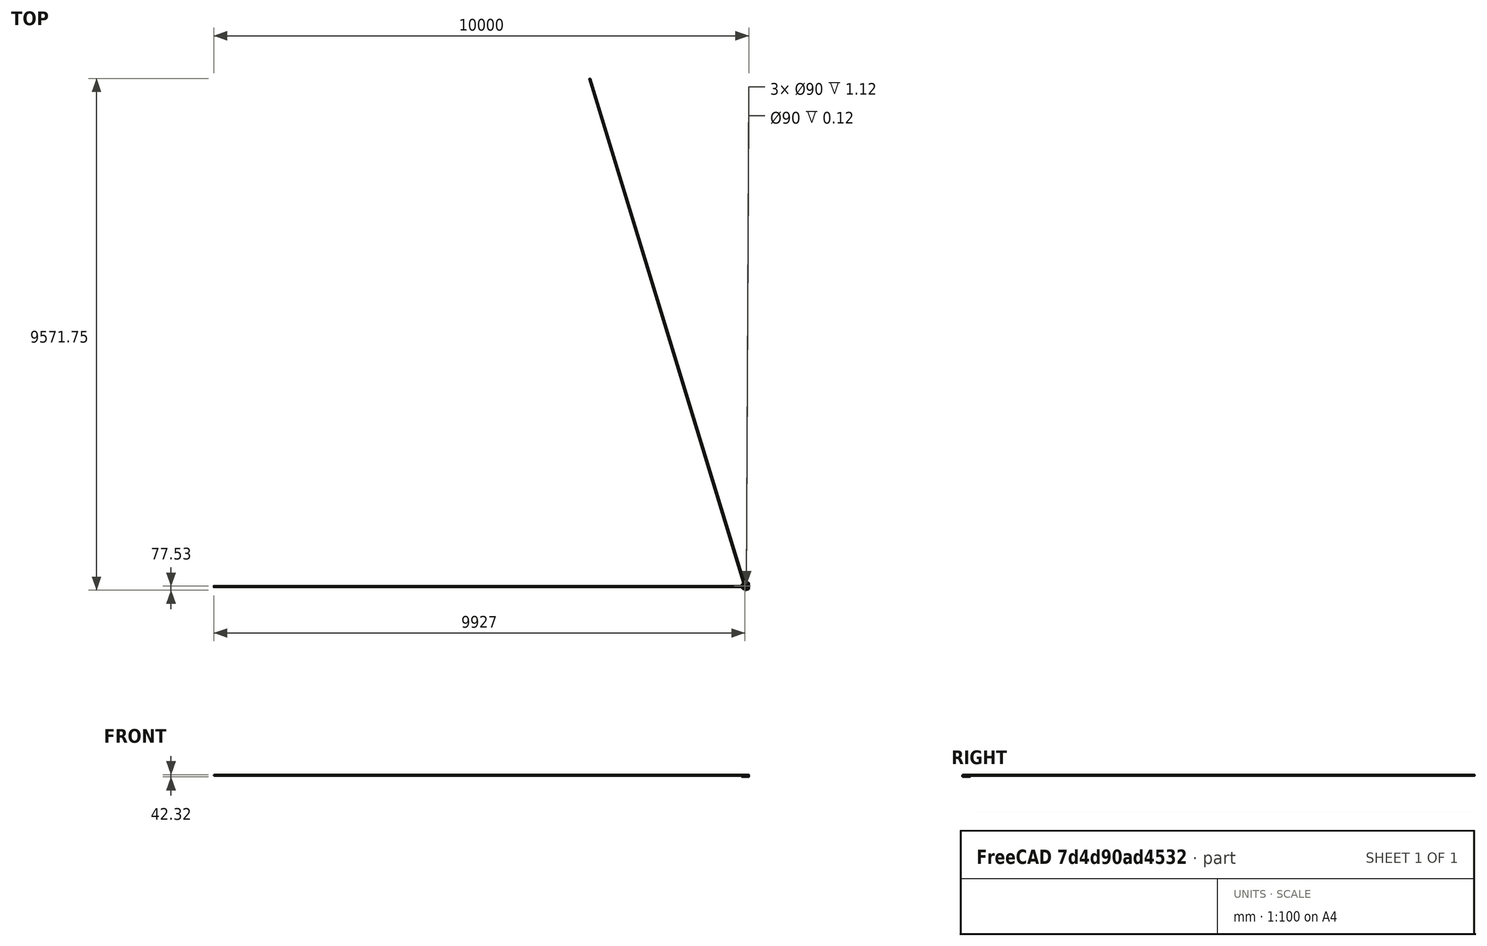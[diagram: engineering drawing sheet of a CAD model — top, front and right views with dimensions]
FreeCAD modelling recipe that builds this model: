
FCSTD DOCUMENT  (FreeCAD 0.16R)
Label: chainguard25TRev1.V4
License: All rights reserved
LicenseURL: http://en.wikipedia.org/wiki/All_rights_reserved
objects: Sketcher::SketchObject×10, PartDesign::Fillet×8, PartDesign::Pad×5, PartDesign::Pocket×5, Part::FeaturePython×3, Mesh::Feature×3
note: 41 computed .brp shape members not serialized (recipe doc carries the construction recipe); baked Part::Feature solids carry a one-line shape summary decoded from their .brp

FEATURE [Sketcher::SketchObject] Sketch001
  sketch-geometry (7):
    g0: LineSegment StartX=60 StartY=64 StartZ=0 EndX=0 EndY=64 EndZ=0
    g1: LineSegment StartX=60 StartY=-64 StartZ=0 EndX=0 EndY=-64 EndZ=0
    g2: ArcOfCircle CenterX=8.21903e-05 CenterY=0 CenterZ=0 NormalX=0 NormalY=0 NormalZ=1 Radius=64 StartAngle=1.5708 EndAngle=4.71239
    g3: Circle CenterX=0 CenterY=0 CenterZ=0 NormalX=0 NormalY=0 NormalZ=1 Radius=45
    g4: ArcOfCircle CenterX=60 CenterY=51 CenterZ=0 NormalX=0 NormalY=0 NormalZ=1 Radius=13 StartAngle=0 EndAngle=1.5708
    g5: ArcOfCircle CenterX=60 CenterY=-51 CenterZ=0 NormalX=0 NormalY=0 NormalZ=1 Radius=13 StartAngle=4.71239 EndAngle=6.28319
    g6: LineSegment StartX=73 StartY=51 StartZ=0 EndX=73 EndY=-51 EndZ=0
  constraints (23):
    c: Horizontal(g0)
    c: Horizontal(g1)
    c: Coincident(g2,g1)
    c: Coincident(g0,g2)
    c: DistanceX(g1,g0) = 0
    c: Equal(g0,g1)
    c: DistanceY(g1,g0) = 128
    c: Radius(g2) = 64
    c: Symmetric(g1,g0,g-1)
    c: Radius(g3) = 45
    c: Coincident(g3,g-1)
    c: PointOnObject(g4,g0)
    c: Radius(g4) = 13
    c: DistanceX(g0,g0) = 60
    c: Equal(g5,g4)
    c: Vertical(g6)
    c: DistanceX(g-1,g6) = 73
    c: Symmetric(g6,g6,g-1)
    c: DistanceY(g6,g6) = 102
    c: Coincident(g4,g6)
    c: Coincident(g5,g6)
    c: Coincident(g1,g5)
    c: Coincident(g0,g4)
FEATURE [PartDesign::Pad] Pad  label="Faceplate"
  Length = 1.12
  Length2 = 100
  Reversed = true
  Sketch = -> Sketch001
  Type = 0
FEATURE [Sketcher::SketchObject] Sketch002
  sketch-geometry (8):
    g0: LineSegment StartX=60 StartY=64 StartZ=0 EndX=0 EndY=64 EndZ=0
    g1: LineSegment StartX=60 StartY=-64 StartZ=0 EndX=0 EndY=-64 EndZ=0
    g2: ArcOfCircle CenterX=6.44712e-05 CenterY=0 CenterZ=0 NormalX=0 NormalY=0 NormalZ=1 Radius=64 StartAngle=1.5708 EndAngle=4.71239
    g3: LineSegment StartX=0 StartY=62 StartZ=0 EndX=60 EndY=62 EndZ=0
    g4: LineSegment StartX=0 StartY=-62 StartZ=0 EndX=60 EndY=-62 EndZ=0
    g5: LineSegment StartX=60 StartY=64 StartZ=0 EndX=60 EndY=62 EndZ=0
    g6: LineSegment StartX=60 StartY=-62 StartZ=0 EndX=60 EndY=-64 EndZ=0
    g7: ArcOfCircle CenterX=1.45954e-05 CenterY=0 CenterZ=0 NormalX=0 NormalY=0 NormalZ=1 Radius=62 StartAngle=1.5708 EndAngle=4.71239
  constraints (25):
    c: Horizontal(g0)
    c: Horizontal(g1)
    c: Coincident(g2,g1)
    c: Coincident(g0,g2)
    c: DistanceX(g1,g0) = 0
    c: Equal(g0,g1)
    c: DistanceY(g1,g0) = 128
    c: Radius(g2) = 64
    c: Symmetric(g1,g0,g-1)
    c: Radius(g7) = 62
    c: Parallel(g0,g3)
    c: DistanceY(g3,g0) = 2
    c: DistanceY(g1,g4) = 2
    c: Parallel(g4,g1)
    c: DistanceX(g0,g3) = 0
    c: DistanceX(g4) = 0
    c: DistanceX(g0) = 60
    c: Equal(g3,g0)
    c: Equal(g4,g0)
    c: Coincident(g4,g6)
    c: Coincident(g6,g1)
    c: Coincident(g5,g3)
    c: Coincident(g5,g0)
    c: Coincident(g7,g3)
    c: Coincident(g7,g4)
FEATURE [PartDesign::Pad] Pad001  label="Connector"
  Length = 8
  Length2 = 100
  Sketch = -> Sketch002
  Type = 0
FEATURE [Sketcher::SketchObject] Sketch004  label="BossST"
  sketch-geometry (5):
    g0: LineSegment StartX=41.8431 StartY=-62 StartZ=0 EndX=1.8431 EndY=-62 EndZ=0
    g1: LineSegment StartX=1.8431 StartY=-62 StartZ=0 EndX=1.8431 EndY=-75.5264 EndZ=0
    g2: LineSegment StartX=41.8431 StartY=-66 StartZ=0 EndX=41.8431 EndY=-62 EndZ=0
    g3: LineSegment StartX=4.42785 StartY=-77.439 StartZ=0 EndX=41.8431 EndY=-66 EndZ=0
    g4: ArcOfCircle CenterX=3.8431 CenterY=-75.5264 CenterZ=0 NormalX=0 NormalY=0 NormalZ=1 Radius=2 StartAngle=3.14159 EndAngle=5.00909
  constraints (13):
    c: Coincident(g0,g1)
    c: Vertical(g1)
    c: Vertical(g2)
    c: DistanceX(g0,g0) = 40
    c: Angle(g3) = 0.296706
    c: DistanceY(g0,g-1) = 62
    c: Horizontal(g0)
    c: DistanceY(g2,g2) = 4
    c: Coincident(g2,g0)
    c: Coincident(g3,g2)
    c: Tangent(g3,g4) = -1.5708
    c: Tangent(g1,g4) = -1.5708
    c: Radius(g4) = 2
FEATURE [Sketcher::SketchObject] Sketch
  Support = -> Pad [Face8]
  sketch-geometry (4):
    g0: LineSegment StartX=65 StartY=35 StartZ=0 EndX=73 EndY=35 EndZ=0
    g1: LineSegment StartX=73 StartY=35 StartZ=0 EndX=73 EndY=-35 EndZ=0
    g2: LineSegment StartX=73 StartY=-35 StartZ=0 EndX=65 EndY=-35 EndZ=0
    g3: LineSegment StartX=65 StartY=-35 StartZ=0 EndX=65 EndY=35 EndZ=0
  constraints (12):
    c: Coincident(g0,g1)
    c: Coincident(g1,g2)
    c: Coincident(g2,g3)
    c: Coincident(g3,g0)
    c: Horizontal(g0)
    c: Horizontal(g2)
    c: Vertical(g1)
    c: Vertical(g3)
    c: Symmetric(g0,g2,g-1)
    c: DistanceX(g0,g0) = 8
    c: DistanceX(g-1,g0) = 73
    c: DistanceY(g3,g3) = 70
FEATURE [PartDesign::Pad] Pad003  label="SyncStiffener"
  Length = 3
  Length2 = 100
  Sketch = -> Sketch
  Type = 0
FEATURE [Sketcher::SketchObject] Sketch008
  Placement = pos=(0,0,3) rot=(0,0,1;0rad)
  Support = -> Pad003 [Face14]
  sketch-geometry (4):
    g0: LineSegment StartX=67 StartY=10.5 StartZ=0 EndX=73 EndY=10.5 EndZ=0
    g1: LineSegment StartX=73 StartY=10.5 StartZ=0 EndX=73 EndY=-24.5 EndZ=0
    g2: LineSegment StartX=73 StartY=-24.5 StartZ=0 EndX=67 EndY=-24.5 EndZ=0
    g3: LineSegment StartX=67 StartY=-24.5 StartZ=0 EndX=67 EndY=10.5 EndZ=0
  constraints (12):
    c: Coincident(g0,g1)
    c: Coincident(g1,g2)
    c: Coincident(g2,g3)
    c: Coincident(g3,g0)
    c: Horizontal(g0)
    c: Horizontal(g2)
    c: Vertical(g1)
    c: Vertical(g3)
    c: DistanceX(g0) = 73
    c: DistanceX(g0,g0) = 6
    c: DistanceY(g1,g1) = 35
    c: DistanceY(g-1,g0) = 10.5
FEATURE [PartDesign::Pad] Pad004  label="SyncTubeBoss"
  Length = 27
  Length2 = 100
  Sketch = -> Sketch008
  Type = 0
FEATURE [Sketcher::SketchObject] Sketch009
  ExternalGeometry = -> [Pad004]
  Placement = pos=(73,0,0) rot=(0.57735,0.57735,0.57735;2.0944rad)
  Support = -> Pad004 [Face15]
  sketch-geometry (1):
    g0: Circle CenterX=-7 CenterY=30 CenterZ=0 NormalX=0 NormalY=0 NormalZ=1 Radius=11.2
  constraints (3):
    c: DistanceY(g-1,g0) = 30
    c: Radius(g0) = 11.2
    c: Symmetric(g-3,g-4,g0)
FEATURE [PartDesign::Pad] Pad005  label="ST Boss"
  Length = 30
  Length2 = 100
  Sketch = -> Sketch004
  Type = 0
FEATURE [Sketcher::SketchObject] Sketch005
  Placement = pos=(22.0436,-72.1013,0) rot=(0.978386,0.146221,0.146221;1.59265rad)
  Support = -> Pad005 [Face3]
  sketch-geometry (1):
    g0: Circle CenterX=0 CenterY=30 CenterZ=0 NormalX=0 NormalY=0 NormalZ=1 Radius=11.2
  constraints (3):
    c: Radius(g0) = 11.2
    c: DistanceY(g-1,g0) = 30
    c: PointOnObject(g0,g-2)
FEATURE [PartDesign::Pocket] Pocket
  Length = 5
  Sketch = -> Sketch005
  Type = 1
FEATURE [Sketcher::SketchObject] Sketch007
  Placement = pos=(0,0,30) rot=(0,0,1;0rad)
  Support = -> Pocket [Face4]
  sketch-geometry (4):
    g0: LineSegment StartX=-4.66376 StartY=-53.9533 StartZ=0 EndX=-5.90948 EndY=-71.4649 EndZ=0
    g1: LineSegment StartX=-5.90948 StartY=-71.4649 StartZ=0 EndX=38.1328 EndY=-58 EndZ=0
    g2: LineSegment StartX=38.1328 StartY=-58 StartZ=0 EndX=37.116 EndY=-54.0061 EndZ=0
    g3: LineSegment StartX=37.116 StartY=-54.0061 StartZ=0 EndX=-4.66376 EndY=-53.9533 EndZ=0
  constraints (12):
    c: Coincident(g0,g1)
    c: Coincident(g1,g2)
    c: Coincident(g2,g3)
    c: Coincident(g0,g3)
    c: Distance(g3) = 41.7798
    c: Distance(g0) = 17.5559
    c: Distance(g1) = 46.0546
    c: Distance(g2) = 4.12132
    c: DistanceX(g0,g-1) = 4.66376
    c: DistanceX(g0,g-1) = 5.90948
    c: DistanceY(g2,g-1) = 54.0061
    c: DistanceX(g1) = 38.1328
FEATURE [PartDesign::Pocket] Pocket006
  Length = 22
  Sketch = -> Sketch007
  Type = 0
FEATURE [Sketcher::SketchObject] Sketch012
  ExternalGeometry = -> [Pocket006]
  Placement = pos=(0,0,30) rot=(0,0,1;0rad)
  Support = -> Pocket006 [Face11]
  sketch-geometry (2):
    g0: Circle CenterX=7.76478 CenterY=-73.2817 CenterZ=0 NormalX=0 NormalY=0 NormalZ=1 Radius=1.4
    g1: Circle CenterX=34.5413 CenterY=-65.0953 CenterZ=0 NormalX=0 NormalY=0 NormalZ=1 Radius=1.4
  constraints (6):
    c: Radius(g1) = 1.4
    c: Equal(g1,g0)
    c: Distance(g0,g1) = 28
    c: Distance(g0,g-6) = 3
    c: Distance(g1,g-5) = 3
    c: Distance(g0,g-3) = 2.8
FEATURE [PartDesign::Pocket] Pocket007
  Length = 12
  Sketch = -> Sketch012
  Type = 0
FEATURE [PartDesign::Pocket] Pocket008
  Length = 5
  Sketch = -> Sketch009
  Type = 1
FEATURE [Sketcher::SketchObject] Sketch013
  ExternalGeometry = -> [Pocket008]
  Placement = pos=(0,0,30) rot=(0,0,1;0rad)
  Support = -> Pocket008 [Face21]
  sketch-geometry (2):
    g0: Circle CenterX=70 CenterY=7 CenterZ=0 NormalX=0 NormalY=0 NormalZ=1 Radius=1.4
    g1: Circle CenterX=70 CenterY=-21 CenterZ=0 NormalX=0 NormalY=0 NormalZ=1 Radius=1.4
  constraints (6):
    c: Radius(g0) = 1.4
    c: Equal(g0,g1)
    c: Distance(g0,g1) = 28
    c: Distance(g0,g-4) = 3
    c: Distance(g1,g-6) = 3
    c: Distance(g0,g-3) = 2.8
FEATURE [PartDesign::Pocket] Pocket009
  Length = 15
  Sketch = -> Sketch013
  Type = 0
FEATURE [PartDesign::Fillet] Fillet
  Base = -> Pocket009 [Edge4,Edge12,Edge20,Edge21,Edge22,Edge6,Edge23]
  Radius = 1
FEATURE [PartDesign::Fillet] Fillet001
  Base = -> Pad001 [Edge13,Edge24]
  Radius = 6
FEATURE [PartDesign::Fillet] Fillet002
  Base = -> Fillet001 [Edge4]
  Radius = 1
FEATURE [PartDesign::Fillet] Fillet003
  Base = -> Pocket007 [Edge10]
  Radius = 2
FEATURE [PartDesign::Fillet] Fillet004
  Base = -> Fillet003 [Edge19]
  Radius = 2
FEATURE [PartDesign::Fillet] Fillet005
  Base = -> Fillet004 [Edge31]
  Radius = 1
FEATURE [PartDesign::Fillet] Fillet006
  Base = -> Fillet005 [Edge4]
  Radius = 1
FEATURE [PartDesign::Fillet] Fillet007
  Base = -> Fillet [Edge39,Edge42]
  Radius = 2
FEATURE [Part::FeaturePython] refine  label="refine_Fillet007"  # WARN: FeaturePython — macro-defined, semantics opaque (R4)
  Base = -> Fillet007
FEATURE [Part::FeaturePython] refine001  label="refine_Fillet006"  # WARN: FeaturePython — macro-defined, semantics opaque (R4)
  Base = -> Fillet006
FEATURE [Part::FeaturePython] refine002  label="refine_Fillet002"  # WARN: FeaturePython — macro-defined, semantics opaque (R4)
  Base = -> Fillet002
FEATURE [Mesh::Feature] Mesh  label="refine_Fillet007 (Meshed)"
FEATURE [Mesh::Feature] Mesh001  label="refine_Fillet006 (Meshed)"
FEATURE [Mesh::Feature] Mesh002  label="refine_Fillet002 (Meshed)"
